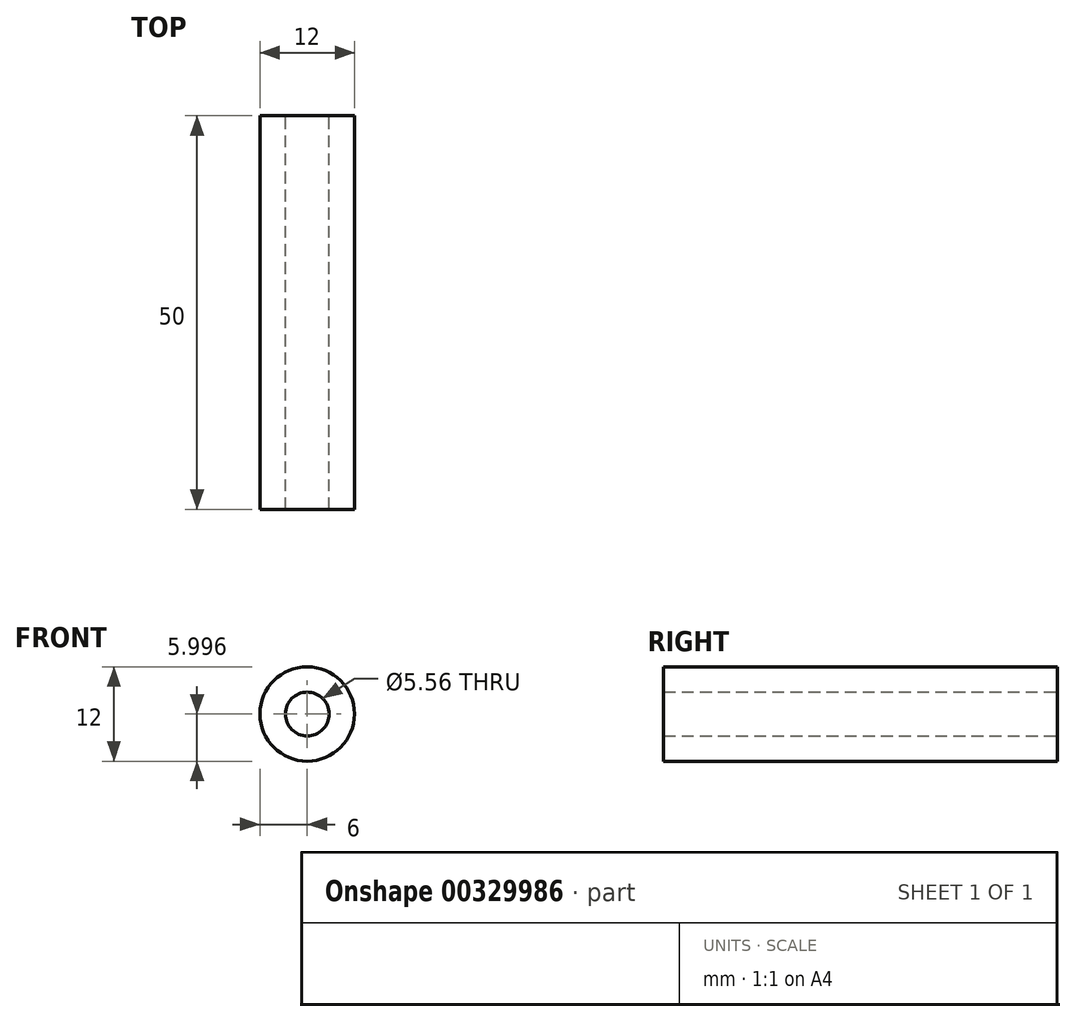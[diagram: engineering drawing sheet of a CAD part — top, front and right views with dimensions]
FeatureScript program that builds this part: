
annotation { "Feature Type Name" : "Feature", "Feature Type Description" : "" }
export const myFeature = defineFeature(function(context is Context, id is Id, definition is map)
    precondition{}
    {
        {
            var Q0;
            Q0=qCreatedBy(makeId("Front.planeOp"),FACE);
            var sketch = newSketch(context, id + "F0", { "sketchPlane" : qUnion([Q0])});
            skCircle(sketch, "E0", {"center": v(0, 5.29) * mm, "radius": 2.78 * mm});
            skCircle(sketch, "E1", {"center": v(0, 5.29) * mm, "radius": 6 * mm});
            skSolve(sketch);
        }
        {
            var Q0;
            Q0=makeQuery(id+"F0.imprint","IMPRINT",FACE,{"disambiguationData":[TD([[makeQuery(id+"F0.imprint","IMPRINT",EDGE,{"derivedFrom":sQuery(id+"F0.wireOp",EDGE,"E0")}),-1.0]])]});
            extrude(context, id + "F1", {"entities" : qUnion([Q0]), "endBound" : BoundingType.SYMMETRIC, "depth" : 50 * mm});
        }
    });
